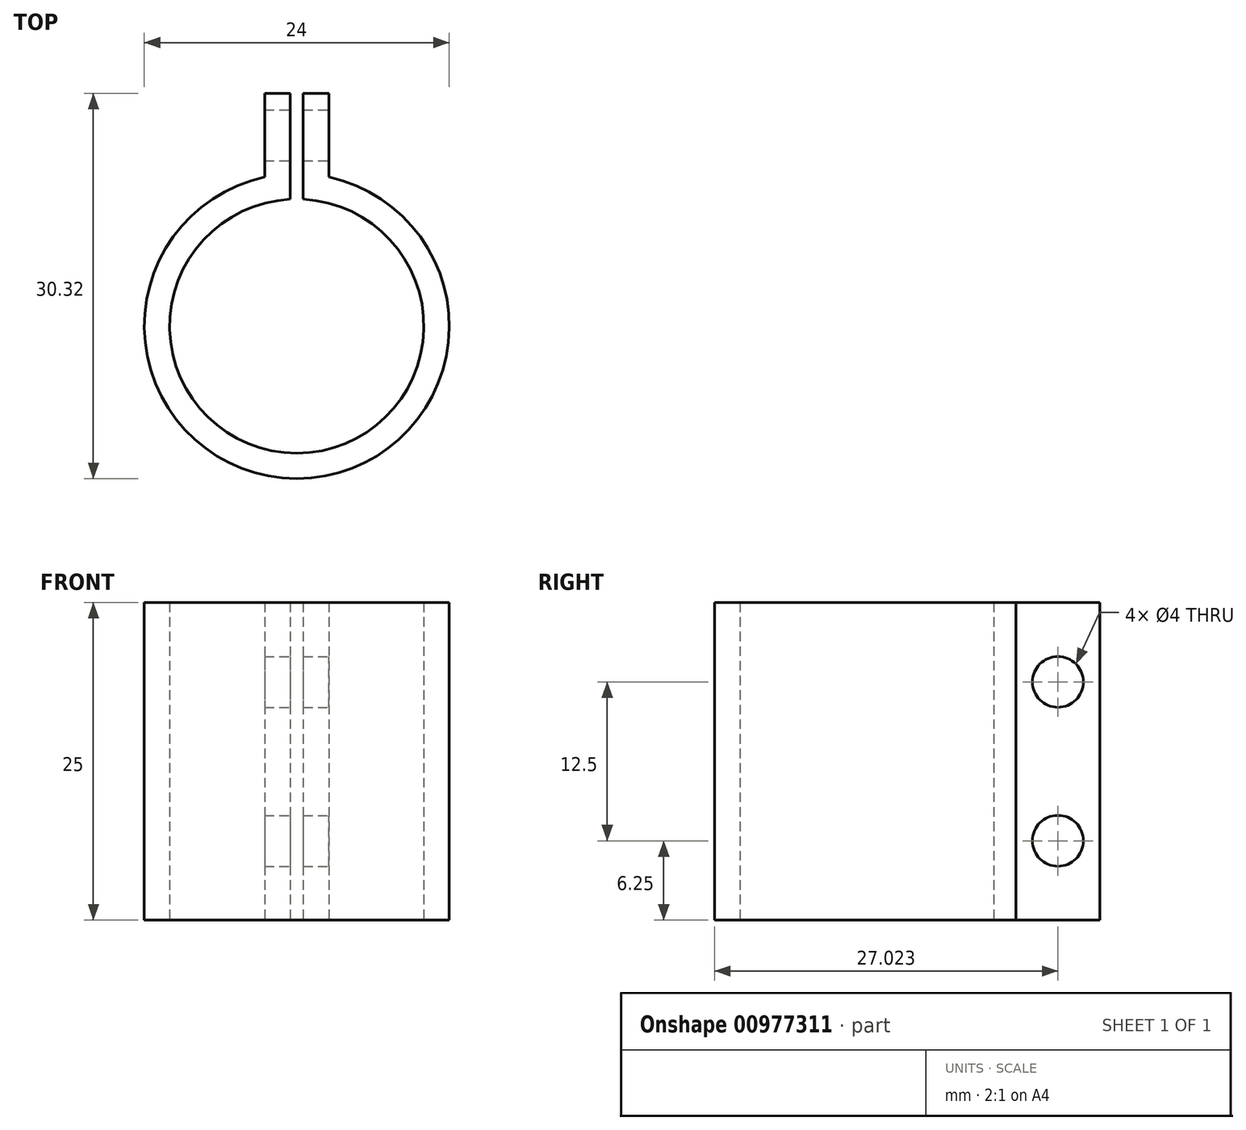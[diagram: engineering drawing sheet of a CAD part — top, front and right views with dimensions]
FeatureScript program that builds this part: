
annotation { "Feature Type Name" : "Feature", "Feature Type Description" : "" }
export const myFeature = defineFeature(function(context is Context, id is Id, definition is map)
    precondition{}
    {
        {
            var Q0;
            Q0=qCreatedBy(makeId("Top.planeOp"),FACE);
            var sketch = newSketch(context, id + "F0", { "sketchPlane" : qUnion([Q0])});
            skCircle(sketch, "E0", {"center": v(0, 0) * mm, "radius": 10 * mm});
            skCircle(sketch, "E1", {"center": v(0, 0) * mm, "radius": 12 * mm});
            skLineSegment(sketch, "E2.bottom", {"start": v(0, 0) * mm, "end": v(-0.5, 0) * mm});
            skLineSegment(sketch, "E2.top", {"start": v(0, 16.04) * mm, "end": v(-0.5, 16.04) * mm});
            skLineSegment(sketch, "E2.left", {"start": v(0, 0) * mm, "end": v(0, 16.04) * mm});
            skLineSegment(sketch, "E2.right", {"start": v(-0.5, 0) * mm, "end": v(-0.5, 16.04) * mm});
            skLineSegment(sketch, "E3.MirrorCS", {"start": v(0, 16.04) * mm, "end": v(0.5, 16.04) * mm});
            skLineSegment(sketch, "E4.MirrorCS", {"start": v(0.5, 0) * mm, "end": v(0.5, 16.04) * mm});
            skLineSegment(sketch, "E5.MirrorCS", {"start": v(0, 0) * mm, "end": v(0.5, 0) * mm});
            skLineSegment(sketch, "E6", {"start": v(-0.5, 0) * mm, "end": v(-2.53, 0) * mm});
            skLineSegment(sketch, "E7", {"start": v(-2.53, 0) * mm, "end": v(-2.53, 18.32) * mm});
            skLineSegment(sketch, "E8", {"start": v(-2.53, 18.32) * mm, "end": v(-0.5, 18.32) * mm});
            skLineSegment(sketch, "E9.MirrorCS", {"start": v(0.5, 0) * mm, "end": v(2.53, 0) * mm});
            skLineSegment(sketch, "E10.MirrorCS", {"start": v(2.53, 0) * mm, "end": v(2.53, 18.32) * mm});
            skLineSegment(sketch, "E11.MirrorCS", {"start": v(2.53, 18.32) * mm, "end": v(0.5, 18.32) * mm});
            skLineSegment(sketch, "E12", {"start": v(-0.5, 16.04) * mm, "end": v(-0.5, 18.32) * mm});
            skLineSegment(sketch, "E13", {"start": v(0.5, 16.04) * mm, "end": v(0.5, 18.32) * mm});
            skSolve(sketch);
        }
        {
            var Q0;
            {var subQ0=sQuery(id+"F0.wireOp",EDGE,"E10.MirrorCS");var subQ1=sQuery(id+"F0.wireOp",EDGE,"E0");var subQ2=makeQuery(id+"F0.imprint","INTERSECT",VERTEX,{"derivedFrom":[subQ1,subQ0]});Q0=makeQuery(id+"F0.imprint","IMPRINT",FACE,{"disambiguationData":[TD([[makeQuery(id+"F0.imprint","IMPRINT",EDGE,{"disambiguationData":[TD([[subQ2,1.0]])],"derivedFrom":subQ1}),-1.0]])]});}
            var Q1;
            {var subQ0=sQuery(id+"F0.wireOp",EDGE,"E2.right");var subQ1=sQuery(id+"F0.wireOp",EDGE,"E0");var subQ2=makeQuery(id+"F0.imprint","INTERSECT",VERTEX,{"derivedFrom":[subQ1,subQ0]});Q1=makeQuery(id+"F0.imprint","IMPRINT",FACE,{"disambiguationData":[TD([[makeQuery(id+"F0.imprint","IMPRINT",EDGE,{"disambiguationData":[TD([[subQ2,-1.0]])],"derivedFrom":subQ1}),-1.0]])]});}
            var Q2;
            {var subQ0=sQuery(id+"F0.wireOp",EDGE,"E4.MirrorCS");var subQ1=sQuery(id+"F0.wireOp",EDGE,"E0");var subQ2=makeQuery(id+"F0.imprint","INTERSECT",VERTEX,{"derivedFrom":[subQ1,subQ0]});Q2=makeQuery(id+"F0.imprint","IMPRINT",FACE,{"disambiguationData":[TD([[makeQuery(id+"F0.imprint","IMPRINT",EDGE,{"disambiguationData":[TD([[subQ2,1.0]])],"derivedFrom":subQ1}),-1.0]])]});}
            var Q3;
            {var subQ5=sQuery(id+"F0.wireOp",EDGE,"E11.MirrorCS");Q3=makeQuery(id+"F0.imprint","IMPRINT",FACE,{"disambiguationData":[TD([[makeQuery(id+"F0.imprint","IMPRINT",EDGE,{"derivedFrom":subQ5}),1.0]])]});}
            var Q4;
            {var subQ5=sQuery(id+"F0.wireOp",EDGE,"E8");Q4=makeQuery(id+"F0.imprint","IMPRINT",FACE,{"disambiguationData":[TD([[makeQuery(id+"F0.imprint","IMPRINT",EDGE,{"derivedFrom":subQ5}),-1.0]])]});}
            extrude(context, id + "F1", {"entities" : qUnion([Q0, Q1, Q2, Q3, Q4]), "depth" : 25 * mm, "offsetDistance" : 25 * mm});
        }
        {
            var Q0;
            Q0=makeQuery(id+"F1.opExtrude","SWEPT_FACE",FACE,{"disambiguationData":[OSD([sQuery(id+"F0.wireOp",EDGE,"E10.MirrorCS")])]});
            var sketch = newSketch(context, id + "F2", { "sketchPlane" : qUnion([Q0])});
            skLineSegment(sketch, "E14", {"start": v(15.02, 25) * mm, "end": v(15.02, 0) * mm});
            skLineSegment(sketch, "E15", {"start": v(11.73, 25) * mm, "end": v(11.73, 12.5) * mm});
            skPoint(sketch, "E16", {"position": v(11.73, 18.75) * mm});
            skPoint(sketch, "E17", {"position": v(15.02, 18.75) * mm});
            skLineSegment(sketch, "E18", {"start": v(11.73, 12.5) * mm, "end": v(11.73, 0) * mm});
            skPoint(sketch, "E19", {"position": v(11.73, 6.25) * mm});
            skPoint(sketch, "E20", {"position": v(15.02, 6.25) * mm});
            skSolve(sketch);
        }
        {
            var Q0;
            Q0=sQuery(id+"F2.wireOp",VERTEX,"E17");
            var Q1;
            Q1=sQuery(id+"F2.wireOp",VERTEX,"E20");
            var Q2;
            Q2=makeQuery(id+"F1.opExtrude","SWEPT_BODY",BODY,{"disambiguationData":[OSD([sQuery(id+"F0.wireOp",EDGE,"E0"),sQuery(id+"F0.wireOp",EDGE,"E1"),sQuery(id+"F0.wireOp",EDGE,"E2.right"),sQuery(id+"F0.wireOp",EDGE,"E4.MirrorCS"),sQuery(id+"F0.wireOp",EDGE,"E7"),sQuery(id+"F0.wireOp",EDGE,"E8"),sQuery(id+"F0.wireOp",EDGE,"E10.MirrorCS"),sQuery(id+"F0.wireOp",EDGE,"E11.MirrorCS"),sQuery(id+"F0.wireOp",EDGE,"E12"),sQuery(id+"F0.wireOp",EDGE,"E13")])]});
            hole(context, id + "F3", {"style" : HoleStyle.SIMPLE, "endStyle" : HoleEndStyle.THROUGH, "holeDiameter" : 4 * mm, "majorDiameter" : 5 * mm, "isTappedThrough" : true, "tappedDepth" : 12.7 * mm, "tapClearance" : 3, "startFromSketch" : true, "locations" : qUnion([Q0, Q1]), "scope" : qUnion([Q2])});
        }
    });
